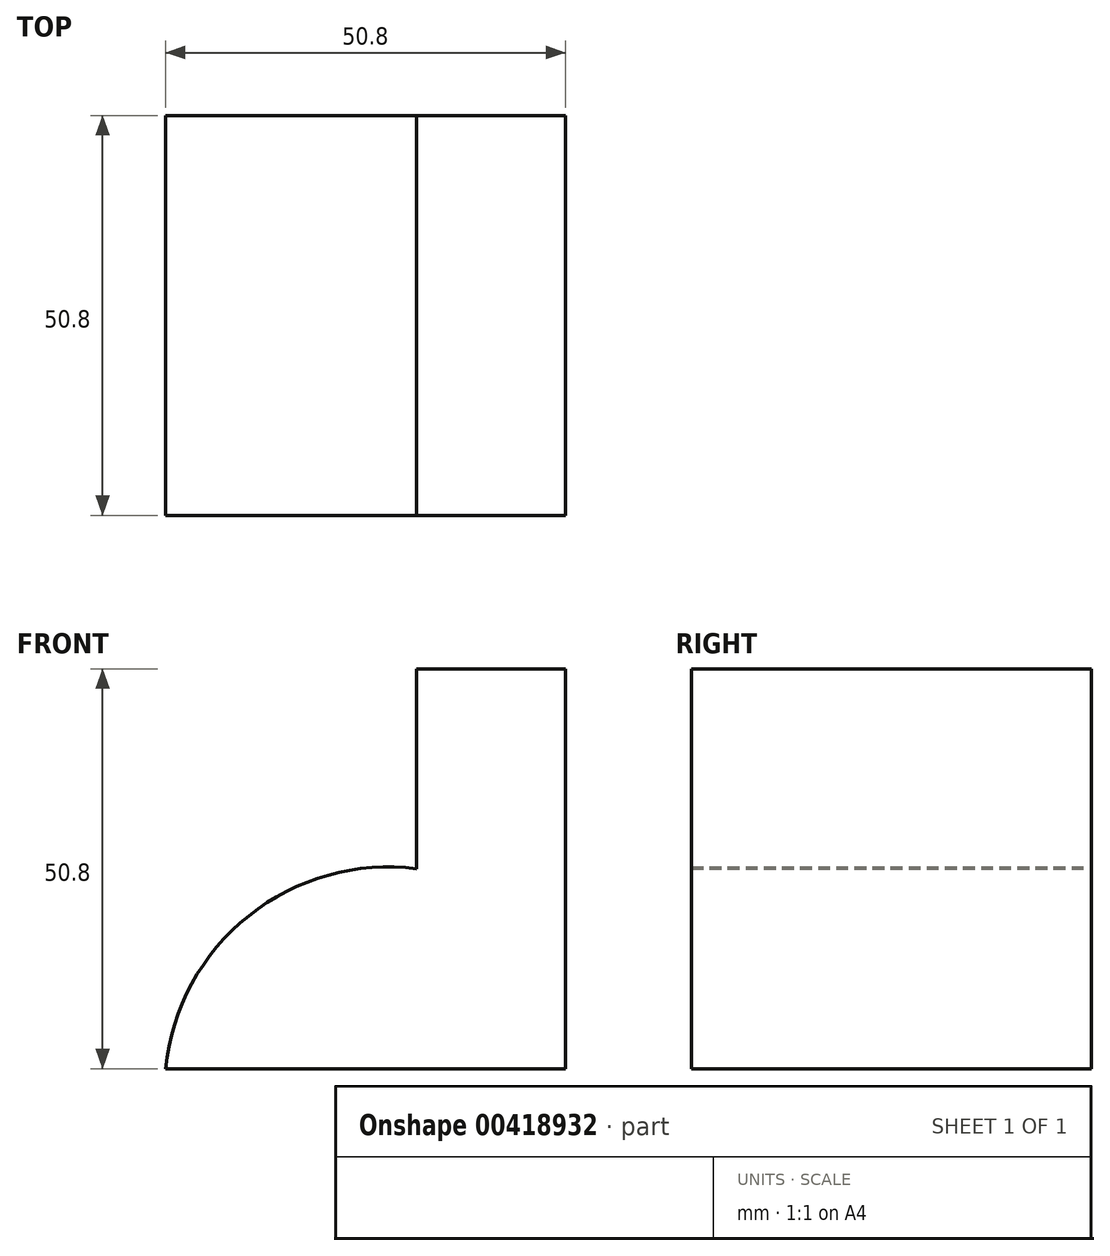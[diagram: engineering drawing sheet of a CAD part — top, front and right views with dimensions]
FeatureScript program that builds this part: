
annotation { "Feature Type Name" : "Feature", "Feature Type Description" : "" }
export const myFeature = defineFeature(function(context is Context, id is Id, definition is map)
    precondition{}
    {
        {
            var Q0;
            Q0=qCreatedBy(makeId("Front.planeOp"),FACE);
            var sketch = newSketch(context, id + "F0", { "sketchPlane" : qUnion([Q0])});
            skLineSegment(sketch, "E0", {"start": v(0, 0) * mm, "end": v(-50.8, 0) * mm});
            skLineSegment(sketch, "E1", {"start": v(0, 0) * mm, "end": v(0, 50.8) * mm});
            skLineSegment(sketch, "E2", {"start": v(0, 50.8) * mm, "end": v(-18.9, 50.8) * mm});
            skLineSegment(sketch, "E3", {"start": v(-18.9, 50.8) * mm, "end": v(-18.9, 25.4) * mm});
            skArc(sketch, "E4", {"start": v(-18.9, 25.4) * mm, "mid": v(-40.22, 19.44) * mm, "end": v(-50.8, 0) * mm});
            skSolve(sketch);
        }
        {
            var Q0;
            Q0 = qSketchRegion(id + "F0", true);
            extrude(context, id + "F1", {"entities" : qUnion([Q0]), "depth" : 50.8 * mm});
        }
    });
